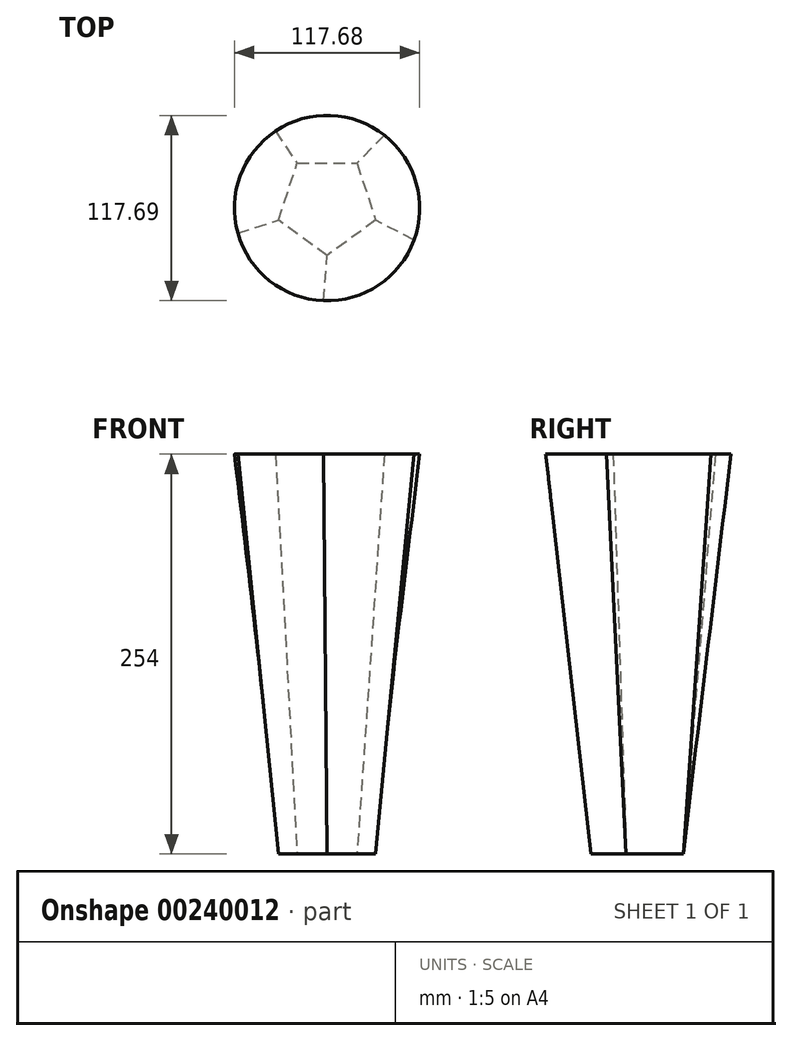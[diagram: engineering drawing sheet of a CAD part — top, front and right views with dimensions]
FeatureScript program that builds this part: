
annotation { "Feature Type Name" : "Feature", "Feature Type Description" : "" }
export const myFeature = defineFeature(function(context is Context, id is Id, definition is map)
    precondition{}
    {
        {
            var Q0;
            Q0=qCreatedBy(makeId("Top.planeOp"),FACE);
            var sketch = newSketch(context, id + "F0", { "sketchPlane" : qUnion([Q0])});
            skCircle(sketch, "E0.cCircle", {"center": v(0, 0) * mm, "radius": 26.22 * mm, "construction": true});
            skLineSegment(sketch, "E0.0", {"start": v(-19.05, 26.22) * mm, "end": v(19.05, 26.22) * mm});
            skLineSegment(sketch, "E0.1", {"start": v(19.05, 26.22) * mm, "end": v(30.82, -10.02) * mm});
            skLineSegment(sketch, "E0.2", {"start": v(30.82, -10.02) * mm, "end": v(0, -32.4) * mm});
            skLineSegment(sketch, "E0.3", {"start": v(0, -32.4) * mm, "end": v(-30.82, -10.02) * mm});
            skLineSegment(sketch, "E0.4", {"start": v(-30.82, -10.02) * mm, "end": v(-19.05, 26.22) * mm});
            skPoint(sketch, "E0.0.midPoint", {"position": v(0, 26.22) * mm});
            skSolve(sketch);
        }
        {
            var Q0;
            Q0=qCreatedBy(makeId("Top.planeOp"),FACE);
            cPlane(context, id + "F1", {"entities" : qUnion([Q0]), "cplaneType" : CPlaneType.OFFSET, "offset" : 254 * mm, "width" : 152.4 * mm, "height" : 152.4 * mm});
        }
        {
            var Q0;
            Q0=qCreatedBy(id+"F1.planeOp",FACE);
            var sketch = newSketch(context, id + "F2", { "sketchPlane" : qUnion([Q0])});
            skCircle(sketch, "E1", {"center": v(0, -2.29) * mm, "radius": 58.84 * mm});
            skSolve(sketch);
        }
        {
            var Q0;
            Q0=makeQuery(id+"F2.imprint","IMPRINT",FACE,{"disambiguationData":[TD([[makeQuery(id+"F2.imprint","IMPRINT",EDGE,{"derivedFrom":sQuery(id+"F2.wireOp",EDGE,"E1")}),1.0]])]});
            var Q1;
            Q1=makeQuery(id+"F0.imprint","IMPRINT",FACE,{"disambiguationData":[TD([[makeQuery(id+"F0.imprint","IMPRINT",EDGE,{"derivedFrom":sQuery(id+"F0.wireOp",EDGE,"E0.0")}),-1.0]])]});
            loft(context, id + "F3", {"sheetProfilesArray" : [{ "sheetProfileEntities" : qUnion([Q0]) }, { "sheetProfileEntities" : qUnion([Q1]) }]});
        }
    });
